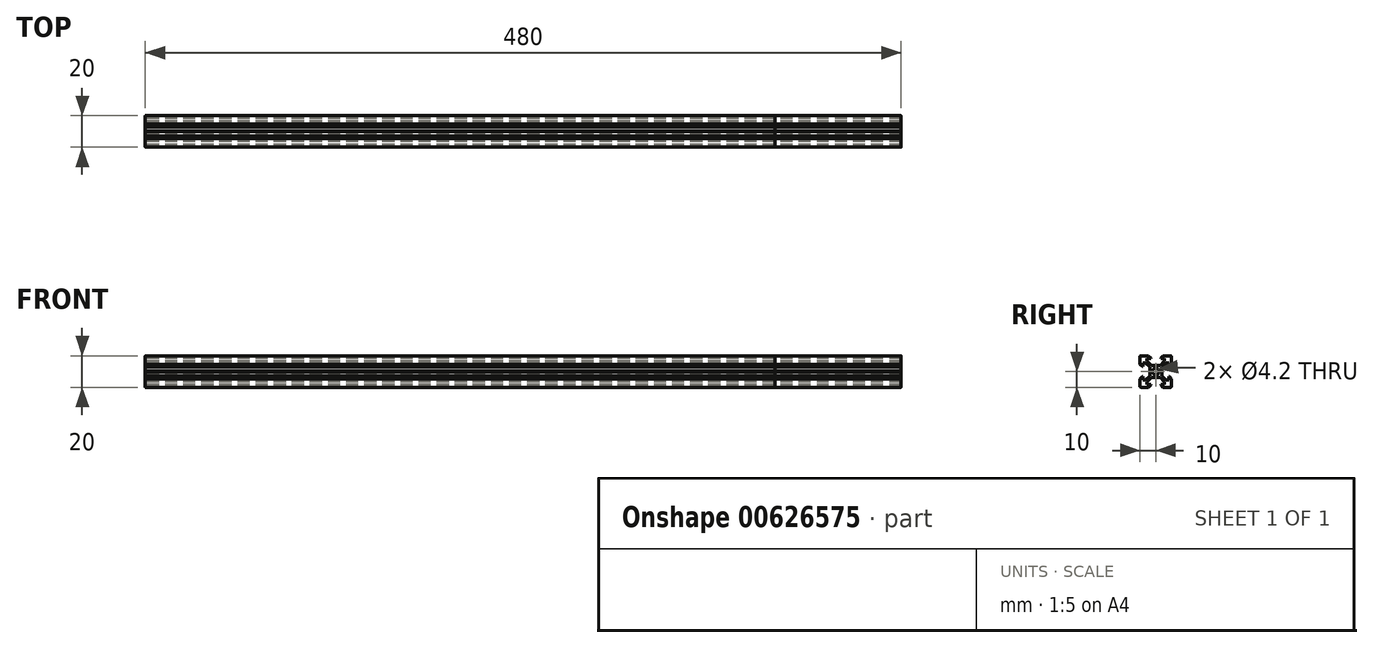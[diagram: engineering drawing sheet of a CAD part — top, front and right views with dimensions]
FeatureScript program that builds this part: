
annotation { "Feature Type Name" : "Feature", "Feature Type Description" : "" }
export const myFeature = defineFeature(function(context is Context, id is Id, definition is map)
    precondition{}
    {
        {
            var Q0;
            Q0=qCreatedBy(makeId("Right.planeOp"),FACE);
            var sketch = newSketch(context, id + "F0", { "sketchPlane" : qUnion([Q0])});
            skArc(sketch, "E0", {"start": v(-10, -9.5) * mm, "mid": v(-9.85, -9.85) * mm, "end": v(-9.5, -10) * mm});
            skCircle(sketch, "E1", {"center": v(0, 0) * mm, "radius": 2.1 * mm});
            skArc(sketch, "E2", {"start": v(-9.5, 10) * mm, "mid": v(-9.85, 9.85) * mm, "end": v(-10, 9.5) * mm});
            skLineSegment(sketch, "E3", {"start": v(-3.69, 0) * mm, "end": v(-3.9, -0.2) * mm});
            skLineSegment(sketch, "E4", {"start": v(-3.9, -0.21) * mm, "end": v(-3.9, -2.84) * mm});
            skLineSegment(sketch, "E5", {"start": v(-3.9, -2.84) * mm, "end": v(-6.56, -5.5) * mm});
            skLineSegment(sketch, "E6", {"start": v(-6.56, -5.5) * mm, "end": v(-8.2, -5.5) * mm});
            skLineSegment(sketch, "E7", {"start": v(-8.2, -5.5) * mm, "end": v(-8.2, -3.12) * mm});
            skLineSegment(sketch, "E8", {"start": v(-8.2, -3.12) * mm, "end": v(-8.54, -3.12) * mm});
            skLineSegment(sketch, "E9", {"start": v(-8.54, -3.12) * mm, "end": v(-10, -4.58) * mm});
            skLineSegment(sketch, "E10", {"start": v(-10, -9.5) * mm, "end": v(-10, -4.58) * mm});
            skLineSegment(sketch, "E11", {"start": v(-9.5, -10) * mm, "end": v(-4.58, -10) * mm});
            skLineSegment(sketch, "E12", {"start": v(-3.12, -8.54) * mm, "end": v(-4.58, -10) * mm});
            skLineSegment(sketch, "E13", {"start": v(-3.12, -8.2) * mm, "end": v(-3.12, -8.54) * mm});
            skLineSegment(sketch, "E14", {"start": v(-5.5, -8.2) * mm, "end": v(-3.12, -8.2) * mm});
            skLineSegment(sketch, "E15", {"start": v(-5.5, -6.56) * mm, "end": v(-5.5, -8.2) * mm});
            skLineSegment(sketch, "E16", {"start": v(-2.84, -3.9) * mm, "end": v(-5.5, -6.56) * mm});
            skLineSegment(sketch, "E17", {"start": v(-0.21, -3.9) * mm, "end": v(-2.84, -3.9) * mm});
            skLineSegment(sketch, "E18", {"start": v(0, -3.69) * mm, "end": v(-0.2, -3.9) * mm});
            skLineSegment(sketch, "E19", {"start": v(0, -3.69) * mm, "end": v(0.2, -3.9) * mm});
            skLineSegment(sketch, "E20", {"start": v(0.21, -3.9) * mm, "end": v(2.84, -3.9) * mm});
            skLineSegment(sketch, "E21", {"start": v(2.84, -3.9) * mm, "end": v(5.5, -6.56) * mm});
            skLineSegment(sketch, "E22", {"start": v(5.5, -6.56) * mm, "end": v(5.5, -8.2) * mm});
            skLineSegment(sketch, "E23", {"start": v(5.5, -8.2) * mm, "end": v(3.12, -8.2) * mm});
            skLineSegment(sketch, "E24", {"start": v(3.12, -8.2) * mm, "end": v(3.12, -8.54) * mm});
            skLineSegment(sketch, "E25", {"start": v(3.12, -8.54) * mm, "end": v(4.58, -10) * mm});
            skLineSegment(sketch, "E26", {"start": v(4.58, -10) * mm, "end": v(9.5, -10) * mm});
            skArc(sketch, "E27", {"start": v(9.5, -10) * mm, "mid": v(9.85, -9.85) * mm, "end": v(10, -9.5) * mm});
            skLineSegment(sketch, "E28", {"start": v(10, -9.5) * mm, "end": v(10, -4.58) * mm});
            skLineSegment(sketch, "E29", {"start": v(8.54, -3.12) * mm, "end": v(10, -4.58) * mm});
            skLineSegment(sketch, "E30", {"start": v(8.2, -3.12) * mm, "end": v(8.54, -3.12) * mm});
            skLineSegment(sketch, "E31", {"start": v(8.2, -5.5) * mm, "end": v(8.2, -3.12) * mm});
            skLineSegment(sketch, "E32", {"start": v(6.56, -5.5) * mm, "end": v(8.2, -5.5) * mm});
            skLineSegment(sketch, "E33", {"start": v(3.9, -2.84) * mm, "end": v(6.56, -5.5) * mm});
            skLineSegment(sketch, "E34", {"start": v(3.9, -0.21) * mm, "end": v(3.9, -2.84) * mm});
            skLineSegment(sketch, "E35", {"start": v(3.69, 0) * mm, "end": v(3.9, -0.2) * mm});
            skLineSegment(sketch, "E36", {"start": v(3.69, 0) * mm, "end": v(3.9, 0.2) * mm});
            skLineSegment(sketch, "E37", {"start": v(3.9, 0.21) * mm, "end": v(3.9, 2.84) * mm});
            skLineSegment(sketch, "E38", {"start": v(3.9, 2.84) * mm, "end": v(6.56, 5.5) * mm});
            skLineSegment(sketch, "E39", {"start": v(6.56, 5.5) * mm, "end": v(8.2, 5.5) * mm});
            skLineSegment(sketch, "E40", {"start": v(8.2, 5.5) * mm, "end": v(8.2, 3.12) * mm});
            skLineSegment(sketch, "E41", {"start": v(8.2, 3.12) * mm, "end": v(8.54, 3.12) * mm});
            skLineSegment(sketch, "E42", {"start": v(8.54, 3.12) * mm, "end": v(10, 4.58) * mm});
            skLineSegment(sketch, "E43", {"start": v(10, 4.58) * mm, "end": v(10, 9.5) * mm});
            skArc(sketch, "E44", {"start": v(10, 9.5) * mm, "mid": v(9.85, 9.85) * mm, "end": v(9.5, 10) * mm});
            skLineSegment(sketch, "E45", {"start": v(4.58, 10) * mm, "end": v(9.5, 10) * mm});
            skLineSegment(sketch, "E46", {"start": v(3.12, 8.54) * mm, "end": v(4.58, 10) * mm});
            skLineSegment(sketch, "E47", {"start": v(3.12, 8.2) * mm, "end": v(3.12, 8.54) * mm});
            skLineSegment(sketch, "E48", {"start": v(5.5, 8.2) * mm, "end": v(3.12, 8.2) * mm});
            skLineSegment(sketch, "E49", {"start": v(5.5, 6.56) * mm, "end": v(5.5, 8.2) * mm});
            skLineSegment(sketch, "E50", {"start": v(2.84, 3.9) * mm, "end": v(5.5, 6.56) * mm});
            skLineSegment(sketch, "E51", {"start": v(0.21, 3.9) * mm, "end": v(2.84, 3.9) * mm});
            skLineSegment(sketch, "E52", {"start": v(0, 3.69) * mm, "end": v(0.2, 3.9) * mm});
            skLineSegment(sketch, "E53", {"start": v(0, 3.69) * mm, "end": v(-0.2, 3.9) * mm});
            skLineSegment(sketch, "E54", {"start": v(-0.21, 3.9) * mm, "end": v(-2.84, 3.9) * mm});
            skLineSegment(sketch, "E55", {"start": v(-2.84, 3.9) * mm, "end": v(-5.5, 6.56) * mm});
            skLineSegment(sketch, "E56", {"start": v(-5.5, 6.56) * mm, "end": v(-5.5, 8.2) * mm});
            skLineSegment(sketch, "E57", {"start": v(-5.5, 8.2) * mm, "end": v(-3.12, 8.2) * mm});
            skLineSegment(sketch, "E58", {"start": v(-3.12, 8.2) * mm, "end": v(-3.12, 8.54) * mm});
            skLineSegment(sketch, "E59", {"start": v(-3.12, 8.54) * mm, "end": v(-4.58, 10) * mm});
            skLineSegment(sketch, "E60", {"start": v(-9.5, 10) * mm, "end": v(-4.58, 10) * mm});
            skLineSegment(sketch, "E61", {"start": v(-10, 4.58) * mm, "end": v(-10, 9.5) * mm});
            skLineSegment(sketch, "E62", {"start": v(-8.54, 3.12) * mm, "end": v(-10, 4.58) * mm});
            skLineSegment(sketch, "E63", {"start": v(-8.2, 3.12) * mm, "end": v(-8.54, 3.12) * mm});
            skLineSegment(sketch, "E64", {"start": v(-8.2, 5.5) * mm, "end": v(-8.2, 3.12) * mm});
            skLineSegment(sketch, "E65", {"start": v(-6.56, 5.5) * mm, "end": v(-8.2, 5.5) * mm});
            skLineSegment(sketch, "E66", {"start": v(-3.9, 2.84) * mm, "end": v(-6.56, 5.5) * mm});
            skLineSegment(sketch, "E67", {"start": v(-3.9, 0.21) * mm, "end": v(-3.9, 2.84) * mm});
            skLineSegment(sketch, "E68", {"start": v(-3.69, 0) * mm, "end": v(-3.9, 0.2) * mm});
            skSolve(sketch);
        }
        {
            var Q0;
            Q0=makeQuery(id+"F0.imprint","IMPRINT",FACE,{"disambiguationData":[TD([[makeQuery(id+"F0.imprint","IMPRINT",EDGE,{"derivedFrom":sQuery(id+"F0.wireOp",EDGE,"E0")}),1.0]])]});
            extrude(context, id + "F1", {"entities" : qUnion([Q0]), "depth" : (456 - 56.2) * mm});
        }
        {
            var Q0;
            Q0=qSketchRegion(id+"F0",true);
            extrude(context, id + "F2", {"entities" : qUnion([Q0]), "depth" : 480 * mm, "offsetDistance" : 25 * mm});
        }
    });
